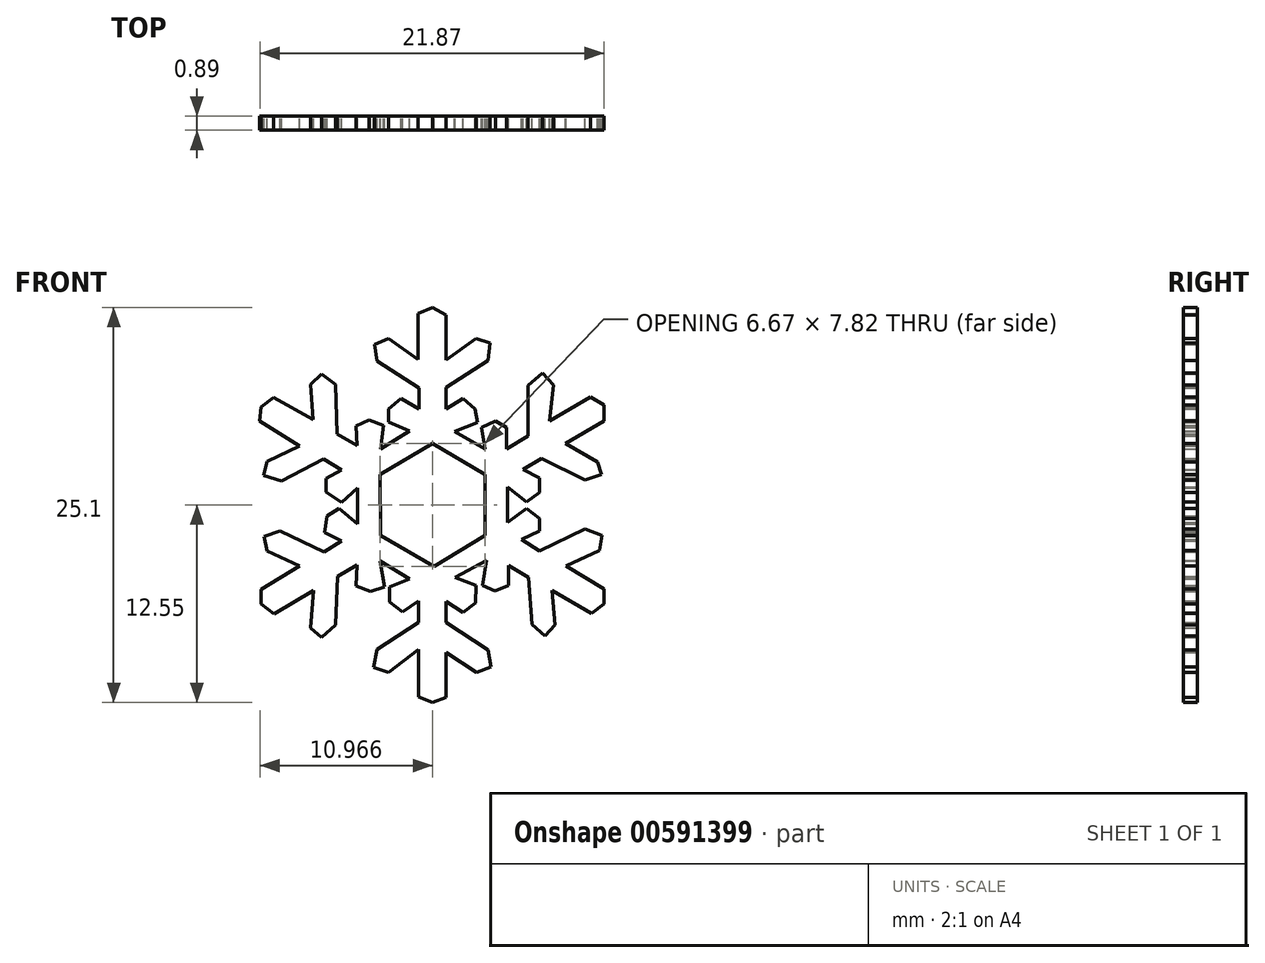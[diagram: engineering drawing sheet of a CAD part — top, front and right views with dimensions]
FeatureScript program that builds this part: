
annotation { "Feature Type Name" : "Feature", "Feature Type Description" : "" }
export const myFeature = defineFeature(function(context is Context, id is Id, definition is map)
    precondition{}
    {
        {
            var Q0;
            Q0=qCreatedBy(makeId("Front.planeOp"),FACE);
            var sketch = newSketch(context, id + "F0", { "sketchPlane" : qUnion([Q0])});
            skLineSegment(sketch, "E0", {"start": v(-14.44, 0.41) * mm, "end": v(-11.12, 2.4) * mm});
            skLineSegment(sketch, "E1", {"start": v(-11.12, 2.4) * mm, "end": v(-7.77, 0.44) * mm});
            skLineSegment(sketch, "E2", {"start": v(-7.77, 0.44) * mm, "end": v(-7.77, -3.45) * mm});
            skLineSegment(sketch, "E3", {"start": v(-7.77, -3.45) * mm, "end": v(-11.02, -5.43) * mm});
            skLineSegment(sketch, "E4", {"start": v(-11.02, -5.43) * mm, "end": v(-14.42, -3.45) * mm});
            skLineSegment(sketch, "E5", {"start": v(-14.42, -3.45) * mm, "end": v(-14.44, 0.41) * mm});
            skLineSegment(sketch, "E6", {"start": v(-9.7, 3.15) * mm, "end": v(-7.77, 2.05) * mm});
            skLineSegment(sketch, "E7", {"start": v(-7.77, 2.05) * mm, "end": v(-7.99, 3.42) * mm});
            skLineSegment(sketch, "E8", {"start": v(-7.99, 3.42) * mm, "end": v(-7.1, 3.8) * mm});
            skLineSegment(sketch, "E9", {"start": v(-7.1, 3.8) * mm, "end": v(-6.42, 3.42) * mm});
            skLineSegment(sketch, "E10", {"start": v(-6.42, 3.42) * mm, "end": v(-6.42, 2.05) * mm});
            skLineSegment(sketch, "E11", {"start": v(-6.42, 2.05) * mm, "end": v(-5.03, 2.86) * mm});
            skLineSegment(sketch, "E12", {"start": v(-5.03, 2.86) * mm, "end": v(-5.03, 6.06) * mm});
            skLineSegment(sketch, "E13", {"start": v(-5.03, 6.06) * mm, "end": v(-4.12, 6.87) * mm});
            skLineSegment(sketch, "E14", {"start": v(-4.12, 6.87) * mm, "end": v(-3.42, 6.1) * mm});
            skLineSegment(sketch, "E15", {"start": v(-3.42, 6.1) * mm, "end": v(-3.68, 3.8) * mm});
            skLineSegment(sketch, "E16", {"start": v(-3.68, 3.8) * mm, "end": v(-1.07, 5.33) * mm});
            skLineSegment(sketch, "E17", {"start": v(-1.07, 5.33) * mm, "end": v(-0.23, 4.85) * mm});
            skLineSegment(sketch, "E18", {"start": v(-0.23, 4.85) * mm, "end": v(-0.23, 3.8) * mm});
            skLineSegment(sketch, "E19", {"start": v(-0.23, 3.8) * mm, "end": v(-2.67, 2.4) * mm});
            skLineSegment(sketch, "E20", {"start": v(-2.67, 2.4) * mm, "end": v(-0.62, 1.22) * mm});
            skLineSegment(sketch, "E21", {"start": v(-0.62, 1.22) * mm, "end": v(-0.37, 0.41) * mm});
            skLineSegment(sketch, "E22", {"start": v(-0.37, 0.41) * mm, "end": v(-1.43, 0.08) * mm});
            skLineSegment(sketch, "E23", {"start": v(-1.43, 0.08) * mm, "end": v(-4.18, 1.45) * mm});
            skLineSegment(sketch, "E24", {"start": v(-4.18, 1.45) * mm, "end": v(-5.35, 0.74) * mm});
            skLineSegment(sketch, "E25", {"start": v(-5.35, 0.74) * mm, "end": v(-4.3, 0.2) * mm});
            skLineSegment(sketch, "E26", {"start": v(-4.3, 0.2) * mm, "end": v(-4.3, -0.73) * mm});
            skLineSegment(sketch, "E27", {"start": v(-4.3, -0.73) * mm, "end": v(-5.13, -1.31) * mm});
            skLineSegment(sketch, "E28", {"start": v(-5.13, -1.31) * mm, "end": v(-6.34, -0.39) * mm});
            skLineSegment(sketch, "E29", {"start": v(-6.34, -0.39) * mm, "end": v(-6.34, -2.61) * mm});
            skLineSegment(sketch, "E30", {"start": v(-6.34, -2.61) * mm, "end": v(-5.13, -1.75) * mm});
            skLineSegment(sketch, "E31", {"start": v(-5.13, -1.75) * mm, "end": v(-4.3, -2.37) * mm});
            skLineSegment(sketch, "E32", {"start": v(-4.3, -2.37) * mm, "end": v(-4.3, -3.18) * mm});
            skLineSegment(sketch, "E33", {"start": v(-4.3, -3.18) * mm, "end": v(-5.44, -3.71) * mm});
            skLineSegment(sketch, "E34", {"start": v(-5.44, -3.71) * mm, "end": v(-4.3, -4.45) * mm});
            skLineSegment(sketch, "E35", {"start": v(-4.3, -4.45) * mm, "end": v(-1.43, -3.03) * mm});
            skLineSegment(sketch, "E36", {"start": v(-1.43, -3.03) * mm, "end": v(-0.36, -3.44) * mm});
            skLineSegment(sketch, "E37", {"start": v(-0.36, -3.44) * mm, "end": v(-0.5, -4.4) * mm});
            skLineSegment(sketch, "E38", {"start": v(-0.5, -4.4) * mm, "end": v(-2.62, -5.4) * mm});
            skLineSegment(sketch, "E39", {"start": v(-2.62, -5.4) * mm, "end": v(-0.2, -6.86) * mm});
            skLineSegment(sketch, "E40", {"start": v(-0.2, -6.86) * mm, "end": v(-0.2, -7.81) * mm});
            skLineSegment(sketch, "E41", {"start": v(-0.2, -7.81) * mm, "end": v(-1.02, -8.4) * mm});
            skLineSegment(sketch, "E42", {"start": v(-1.02, -8.4) * mm, "end": v(-3.5, -6.93) * mm});
            skLineSegment(sketch, "E43", {"start": v(-3.5, -6.93) * mm, "end": v(-3.33, -9.13) * mm});
            skLineSegment(sketch, "E44", {"start": v(-3.33, -9.13) * mm, "end": v(-3.97, -9.84) * mm});
            skLineSegment(sketch, "E45", {"start": v(-3.97, -9.84) * mm, "end": v(-4.8, -9.1) * mm});
            skLineSegment(sketch, "E46", {"start": v(-4.8, -9.1) * mm, "end": v(-5, -6.13) * mm});
            skLineSegment(sketch, "E47", {"start": v(-5, -6.13) * mm, "end": v(-6.3, -5.34) * mm});
            skLineSegment(sketch, "E48", {"start": v(-6.3, -5.34) * mm, "end": v(-6.3, -6.64) * mm});
            skLineSegment(sketch, "E49", {"start": v(-6.3, -6.64) * mm, "end": v(-7.12, -6.98) * mm});
            skLineSegment(sketch, "E50", {"start": v(-7.12, -6.98) * mm, "end": v(-7.93, -6.64) * mm});
            skLineSegment(sketch, "E51", {"start": v(-7.93, -6.64) * mm, "end": v(-7.66, -5.05) * mm});
            skLineSegment(sketch, "E52", {"start": v(-7.66, -5.05) * mm, "end": v(-9.7, -6.13) * mm});
            skLineSegment(sketch, "E53", {"start": v(-9.7, -6.13) * mm, "end": v(-8.35, -6.64) * mm});
            skLineSegment(sketch, "E54", {"start": v(-8.37, -7.74) * mm, "end": v(-9.18, -8.35) * mm});
            skLineSegment(sketch, "E55", {"start": v(-9.18, -8.35) * mm, "end": v(-10.25, -7.64) * mm});
            skLineSegment(sketch, "E56", {"start": v(-10.25, -7.64) * mm, "end": v(-10.25, -8.96) * mm});
            skLineSegment(sketch, "E57", {"start": v(-10.25, -8.96) * mm, "end": v(-7.58, -10.72) * mm});
            skLineSegment(sketch, "E58", {"start": v(-7.58, -10.72) * mm, "end": v(-7.4, -11.8) * mm});
            skLineSegment(sketch, "E59", {"start": v(-7.4, -11.8) * mm, "end": v(-8.32, -12.15) * mm});
            skLineSegment(sketch, "E60", {"start": v(-8.32, -12.15) * mm, "end": v(-10.25, -10.88) * mm});
            skLineSegment(sketch, "E61", {"start": v(-10.25, -13.74) * mm, "end": v(-11.11, -14.07) * mm});
            skPoint(sketch, "E61.endSnap0", {"position": v(-11.11, -14.24) * mm});
            skLineSegment(sketch, "E62", {"start": v(-11.11, -14.07) * mm, "end": v(-11.98, -13.7) * mm});
            skLineSegment(sketch, "E63", {"start": v(-10.25, -13.74) * mm, "end": v(-10.25, -10.88) * mm});
            skLineSegment(sketch, "E64", {"start": v(-11.98, -13.7) * mm, "end": v(-11.98, -10.7) * mm});
            skLineSegment(sketch, "E65", {"start": v(-11.98, -10.7) * mm, "end": v(-13.9, -12.16) * mm});
            skLineSegment(sketch, "E66", {"start": v(-13.9, -12.16) * mm, "end": v(-14.85, -11.83) * mm});
            skLineSegment(sketch, "E67", {"start": v(-14.85, -11.83) * mm, "end": v(-14.62, -10.7) * mm});
            skLineSegment(sketch, "E68", {"start": v(-14.62, -10.7) * mm, "end": v(-11.99, -8.98) * mm});
            skLineSegment(sketch, "E69", {"start": v(-11.99, -8.98) * mm, "end": v(-11.99, -7.6) * mm});
            skLineSegment(sketch, "E70", {"start": v(-11.99, -7.6) * mm, "end": v(-13.02, -8.32) * mm});
            skLineSegment(sketch, "E71", {"start": v(-13.02, -8.32) * mm, "end": v(-13.83, -7.66) * mm});
            skLineSegment(sketch, "E72", {"start": v(-13.83, -7.66) * mm, "end": v(-13.83, -6.72) * mm});
            skLineSegment(sketch, "E73", {"start": v(-13.83, -6.72) * mm, "end": v(-12.57, -6.2) * mm});
            skLineSegment(sketch, "E74", {"start": v(-12.57, -6.2) * mm, "end": v(-14.44, -5.06) * mm});
            skLineSegment(sketch, "E75", {"start": v(-14.44, -5.06) * mm, "end": v(-14.16, -6.72) * mm});
            skLineSegment(sketch, "E76", {"start": v(-14.16, -6.72) * mm, "end": v(-15.03, -7) * mm});
            skLineSegment(sketch, "E77", {"start": v(-15.03, -7) * mm, "end": v(-15.95, -6.66) * mm});
            skLineSegment(sketch, "E78", {"start": v(-15.95, -6.66) * mm, "end": v(-15.9, -5.32) * mm});
            skLineSegment(sketch, "E79", {"start": v(-15.9, -5.32) * mm, "end": v(-17.14, -6.06) * mm});
            skLineSegment(sketch, "E80", {"start": v(-17.14, -6.06) * mm, "end": v(-17.28, -9.15) * mm});
            skLineSegment(sketch, "E81", {"start": v(-17.28, -9.15) * mm, "end": v(-18.17, -9.94) * mm});
            skLineSegment(sketch, "E82", {"start": v(-18.17, -9.94) * mm, "end": v(-18.85, -9.34) * mm});
            skLineSegment(sketch, "E83", {"start": v(-18.85, -9.34) * mm, "end": v(-18.65, -6.95) * mm});
            skLineSegment(sketch, "E84", {"start": v(-18.65, -6.95) * mm, "end": v(-21.17, -8.45) * mm});
            skLineSegment(sketch, "E85", {"start": v(-21.17, -8.45) * mm, "end": v(-22, -7.8) * mm});
            skLineSegment(sketch, "E86", {"start": v(-22, -7.8) * mm, "end": v(-22, -6.89) * mm});
            skLineSegment(sketch, "E87", {"start": v(-22, -6.89) * mm, "end": v(-19.56, -5.4) * mm});
            skLineSegment(sketch, "E88", {"start": v(-19.56, -5.4) * mm, "end": v(-21.6, -4.43) * mm});
            skLineSegment(sketch, "E89", {"start": v(-21.6, -4.43) * mm, "end": v(-21.8, -3.52) * mm});
            skLineSegment(sketch, "E90", {"start": v(-21.8, -3.52) * mm, "end": v(-20.78, -3.15) * mm});
            skLineSegment(sketch, "E91", {"start": v(-20.78, -3.15) * mm, "end": v(-18, -4.49) * mm});
            skLineSegment(sketch, "E92", {"start": v(-18, -4.49) * mm, "end": v(-16.88, -3.8) * mm});
            skLineSegment(sketch, "E93", {"start": v(-16.88, -3.8) * mm, "end": v(-17.96, -3.27) * mm});
            skLineSegment(sketch, "E94", {"start": v(-17.96, -3.27) * mm, "end": v(-17.81, -2.22) * mm});
            skLineSegment(sketch, "E95", {"start": v(-17.81, -2.22) * mm, "end": v(-17.04, -1.75) * mm});
            skLineSegment(sketch, "E96", {"start": v(-17.04, -1.75) * mm, "end": v(-15.86, -2.72) * mm});
            skLineSegment(sketch, "E97", {"start": v(-15.86, -2.72) * mm, "end": v(-15.86, -0.44) * mm});
            skLineSegment(sketch, "E98", {"start": v(-15.86, -0.44) * mm, "end": v(-16.89, -1.36) * mm});
            skLineSegment(sketch, "E99", {"start": v(-16.89, -1.36) * mm, "end": v(-17.85, -0.68) * mm});
            skLineSegment(sketch, "E100", {"start": v(-17.85, -0.68) * mm, "end": v(-17.85, 0.18) * mm});
            skLineSegment(sketch, "E101", {"start": v(-17.85, 0.18) * mm, "end": v(-16.87, 0.7) * mm});
            skLineSegment(sketch, "E102", {"start": v(-16.87, 0.7) * mm, "end": v(-18.02, 1.4) * mm});
            skLineSegment(sketch, "E103", {"start": v(-18.02, 1.4) * mm, "end": v(-20.7, 0) * mm});
            skLineSegment(sketch, "E104", {"start": v(-20.7, 0) * mm, "end": v(-21.88, 0.38) * mm});
            skLineSegment(sketch, "E105", {"start": v(-21.85, 0.35) * mm, "end": v(-21.62, 1.25) * mm});
            skLineSegment(sketch, "E106", {"start": v(-21.62, 1.25) * mm, "end": v(-19.56, 2.24) * mm});
            skLineSegment(sketch, "E107", {"start": v(-19.56, 2.24) * mm, "end": v(-22.07, 3.8) * mm});
            skLineSegment(sketch, "E108", {"start": v(-22.07, 3.8) * mm, "end": v(-22, 4.7) * mm});
            skLineSegment(sketch, "E109", {"start": v(-22, 4.7) * mm, "end": v(-21.21, 5.32) * mm});
            skLineSegment(sketch, "E110", {"start": v(-21.21, 5.32) * mm, "end": v(-18.68, 3.91) * mm});
            skLineSegment(sketch, "E111", {"start": v(-18.68, 3.91) * mm, "end": v(-18.85, 6.14) * mm});
            skLineSegment(sketch, "E112", {"start": v(-18.85, 6.14) * mm, "end": v(-18.17, 6.8) * mm});
            skLineSegment(sketch, "E113", {"start": v(-18.17, 6.8) * mm, "end": v(-17.27, 6.14) * mm});
            skLineSegment(sketch, "E114", {"start": v(-17.27, 6.14) * mm, "end": v(-17.15, 2.99) * mm});
            skLineSegment(sketch, "E115", {"start": v(-17.15, 2.99) * mm, "end": v(-15.9, 2.27) * mm});
            skLineSegment(sketch, "E116", {"start": v(-15.9, 2.27) * mm, "end": v(-15.95, 3.51) * mm});
            skLineSegment(sketch, "E117", {"start": v(-15.95, 3.51) * mm, "end": v(-15.12, 3.87) * mm});
            skLineSegment(sketch, "E118", {"start": v(-15.12, 3.87) * mm, "end": v(-14.22, 3.54) * mm});
            skLineSegment(sketch, "E119", {"start": v(-14.22, 3.54) * mm, "end": v(-14.42, 2.04) * mm});
            skLineSegment(sketch, "E120", {"start": v(-14.42, 2.04) * mm, "end": v(-12.57, 3.17) * mm});
            skLineSegment(sketch, "E121", {"start": v(-12.57, 3.17) * mm, "end": v(-13.9, 3.74) * mm});
            skLineSegment(sketch, "E122", {"start": v(-13.9, 3.74) * mm, "end": v(-13.9, 4.59) * mm});
            skLineSegment(sketch, "E123", {"start": v(-13.9, 4.59) * mm, "end": v(-13.1, 5.23) * mm});
            skLineSegment(sketch, "E124", {"start": v(-13.1, 5.23) * mm, "end": v(-11.97, 4.59) * mm});
            skLineSegment(sketch, "E125", {"start": v(-11.97, 4.59) * mm, "end": v(-11.97, 5.9) * mm});
            skLineSegment(sketch, "E126", {"start": v(-11.97, 5.9) * mm, "end": v(-14.62, 7.61) * mm});
            skLineSegment(sketch, "E127", {"start": v(-14.62, 7.61) * mm, "end": v(-14.8, 8.68) * mm});
            skLineSegment(sketch, "E128", {"start": v(-14.8, 8.68) * mm, "end": v(-13.9, 9.05) * mm});
            skLineSegment(sketch, "E129", {"start": v(-13.9, 9.05) * mm, "end": v(-12.03, 7.74) * mm});
            skLineSegment(sketch, "E130", {"start": v(-12.03, 7.74) * mm, "end": v(-12.03, 10.66) * mm});
            skLineSegment(sketch, "E131", {"start": v(-12.03, 10.66) * mm, "end": v(-11.11, 11.03) * mm});
            skPoint(sketch, "E131.endSnap0", {"position": v(-11.11, 11.16) * mm});
            skLineSegment(sketch, "E132", {"start": v(-11.11, 11.03) * mm, "end": v(-10.24, 10.55) * mm});
            skLineSegment(sketch, "E133", {"start": v(-10.24, 10.55) * mm, "end": v(-10.24, 7.7) * mm});
            skLineSegment(sketch, "E134", {"start": v(-10.24, 7.7) * mm, "end": v(-8.35, 9.05) * mm});
            skLineSegment(sketch, "E135", {"start": v(-8.35, 9.05) * mm, "end": v(-7.44, 8.77) * mm});
            skLineSegment(sketch, "E136", {"start": v(-7.44, 8.77) * mm, "end": v(-7.57, 7.64) * mm});
            skLineSegment(sketch, "E137", {"start": v(-7.57, 7.64) * mm, "end": v(-10.24, 5.94) * mm});
            skLineSegment(sketch, "E138", {"start": v(-10.24, 5.94) * mm, "end": v(-10.24, 4.59) * mm});
            skLineSegment(sketch, "E139", {"start": v(-10.24, 4.59) * mm, "end": v(-9.17, 5.24) * mm});
            skLineSegment(sketch, "E140", {"start": v(-9.17, 5.24) * mm, "end": v(-8.4, 4.59) * mm});
            skLineSegment(sketch, "E141", {"start": v(-8.4, 4.59) * mm, "end": v(-8.25, 3.72) * mm});
            skLineSegment(sketch, "E142", {"start": v(-8.25, 3.72) * mm, "end": v(-9.7, 3.15) * mm});
            skLineSegment(sketch, "E143", {"start": v(-8.35, -6.64) * mm, "end": v(-8.37, -7.74) * mm});
            skLineSegment(sketch, "E144", {"start": v(-13.5, 2.6) * mm, "end": v(-12.78, 1.4) * mm});
            skPoint(sketch, "E144.endSnap0", {"position": v(-12.78, 1.4) * mm});
            skLineSegment(sketch, "E145", {"start": v(-14.22, 3.54) * mm, "end": v(-15.08, 3.87) * mm});
            skSolve(sketch);
        }
        {
            var Q0;
            Q0=makeQuery(id+"F0.imprint","IMPRINT",FACE,{"disambiguationData":[TD([[makeQuery(id+"F0.imprint","IMPRINT",EDGE,{"derivedFrom":sQuery(id+"F0.wireOp",EDGE,"E0")}),1.0]])]});
            extrude(context, id + "F1", {"entities" : qUnion([Q0]), "depth" : 0.89 * mm});
        }
    });
